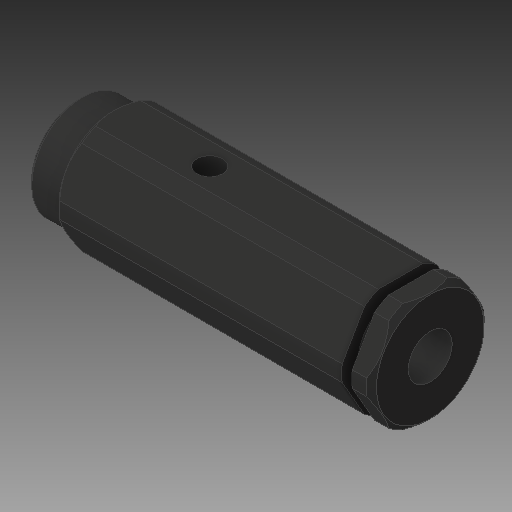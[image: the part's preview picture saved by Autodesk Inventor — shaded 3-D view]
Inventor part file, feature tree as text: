
AUTODESK INVENTOR PART (.ipt)
format: ipt  version: 2017 (Build 210142000, 142)  size: 168,448 bytes
history: native  units: in
note: dims shown in document units (in); Inventor stores cm internally (conversion verified against a paired STEP export)
features: chamfer x1
ambient origin geometry x8: Origin, YZ Plane, XZ Plane, XY Plane, X Axis, Y Axis, Z Axis, Center Point
bodies: Solid1 (feature_tree)
feature tree (1):
  chamfer  "Chamfer1"  [1 undecoded]
note: 1 required parameter value undecoded (feature->parameter linkage not recoverable at this tier; creation-order binding heuristic only, values carry confidence <= 0.55)
